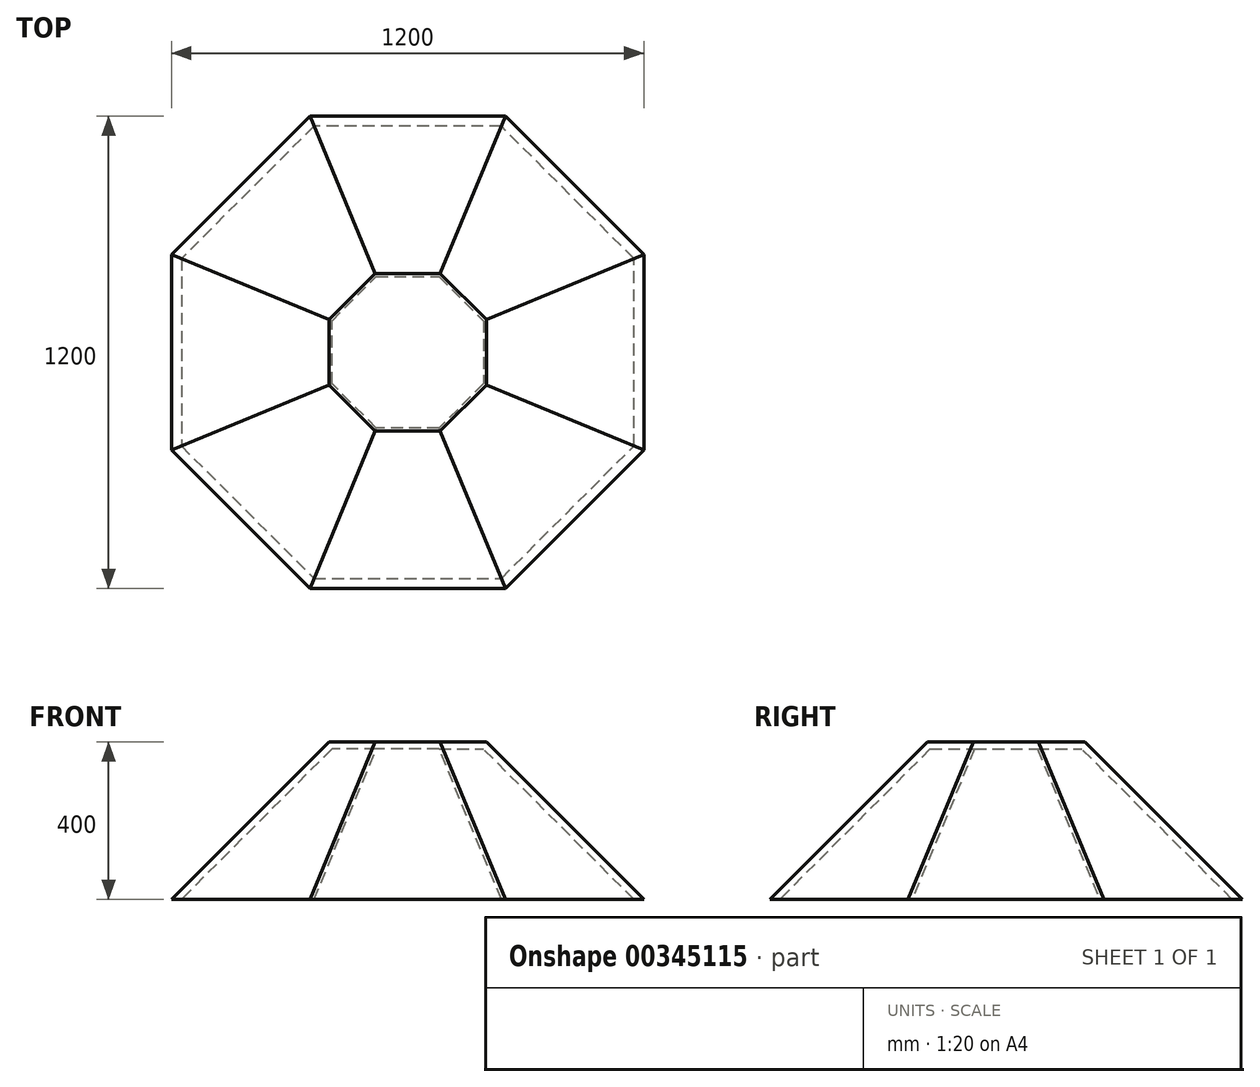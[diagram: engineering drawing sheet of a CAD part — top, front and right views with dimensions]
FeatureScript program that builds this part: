
annotation { "Feature Type Name" : "Feature", "Feature Type Description" : "" }
export const myFeature = defineFeature(function(context is Context, id is Id, definition is map)
    precondition{}
    {
        {
            var Q0;
            Q0=qCreatedBy(makeId("Top.planeOp"),FACE);
            var sketch = newSketch(context, id + "F0", { "sketchPlane" : qUnion([Q0])});
            skCircle(sketch, "E0.cCircle", {"center": v(0, 0) * mm, "radius": 600 * mm, "construction": true});
            skLineSegment(sketch, "E0.0", {"start": v(248.53, -600) * mm, "end": v(-248.53, -600) * mm});
            skLineSegment(sketch, "E0.1", {"start": v(-248.53, -600) * mm, "end": v(-600, -248.53) * mm});
            skLineSegment(sketch, "E0.2", {"start": v(-600, -248.53) * mm, "end": v(-600, 248.53) * mm});
            skLineSegment(sketch, "E0.3", {"start": v(-600, 248.53) * mm, "end": v(-248.53, 600) * mm});
            skLineSegment(sketch, "E0.4", {"start": v(-248.53, 600) * mm, "end": v(248.53, 600) * mm});
            skLineSegment(sketch, "E0.5", {"start": v(248.53, 600) * mm, "end": v(600, 248.53) * mm});
            skLineSegment(sketch, "E0.6", {"start": v(600, 248.53) * mm, "end": v(600, -248.53) * mm});
            skLineSegment(sketch, "E0.7", {"start": v(600, -248.53) * mm, "end": v(248.53, -600) * mm});
            skPoint(sketch, "E0.0.midPoint", {"position": v(0, -600) * mm});
            skSolve(sketch);
        }
        {
            var Q0;
            Q0 = qSketchRegion(id + "F0", true);
            extrude(context, id + "F1", {"entities" : qUnion([Q0]), "depth" : 400 * mm});
        }
        {
            var Q0;
            Q0=makeQuery(id+"F1.opExtrude","CAP_FACE",FACE,{"disambiguationData":[OSD([sQuery(id+"F0.wireOp",EDGE,"E0.0"),sQuery(id+"F0.wireOp",EDGE,"E0.1"),sQuery(id+"F0.wireOp",EDGE,"E0.2"),sQuery(id+"F0.wireOp",EDGE,"E0.3"),sQuery(id+"F0.wireOp",EDGE,"E0.4"),sQuery(id+"F0.wireOp",EDGE,"E0.5"),sQuery(id+"F0.wireOp",EDGE,"E0.6"),sQuery(id+"F0.wireOp",EDGE,"E0.7")])],"isStart":false});
            chamfer(context, id + "F2", {"entities" : qUnion([Q0]), "chamferType" : ChamferType.TWO_OFFSETS, "width1" : 400 * mm, "oppositeDirection" : false, "width2" : 400 * mm, "tangentPropagation" : true});
        }
        {
            var Q0;
            Q0=makeQuery(id+"F1.opExtrude","CAP_FACE",FACE,{"disambiguationData":[OSD([sQuery(id+"F0.wireOp",EDGE,"E0.0"),sQuery(id+"F0.wireOp",EDGE,"E0.1"),sQuery(id+"F0.wireOp",EDGE,"E0.2"),sQuery(id+"F0.wireOp",EDGE,"E0.3"),sQuery(id+"F0.wireOp",EDGE,"E0.4"),sQuery(id+"F0.wireOp",EDGE,"E0.5"),sQuery(id+"F0.wireOp",EDGE,"E0.6"),sQuery(id+"F0.wireOp",EDGE,"E0.7")])],"isStart":true});
            shell(context, id + "F3", {"entities" : qUnion([Q0]), "thickness" : 18 * mm});
        }
    });
